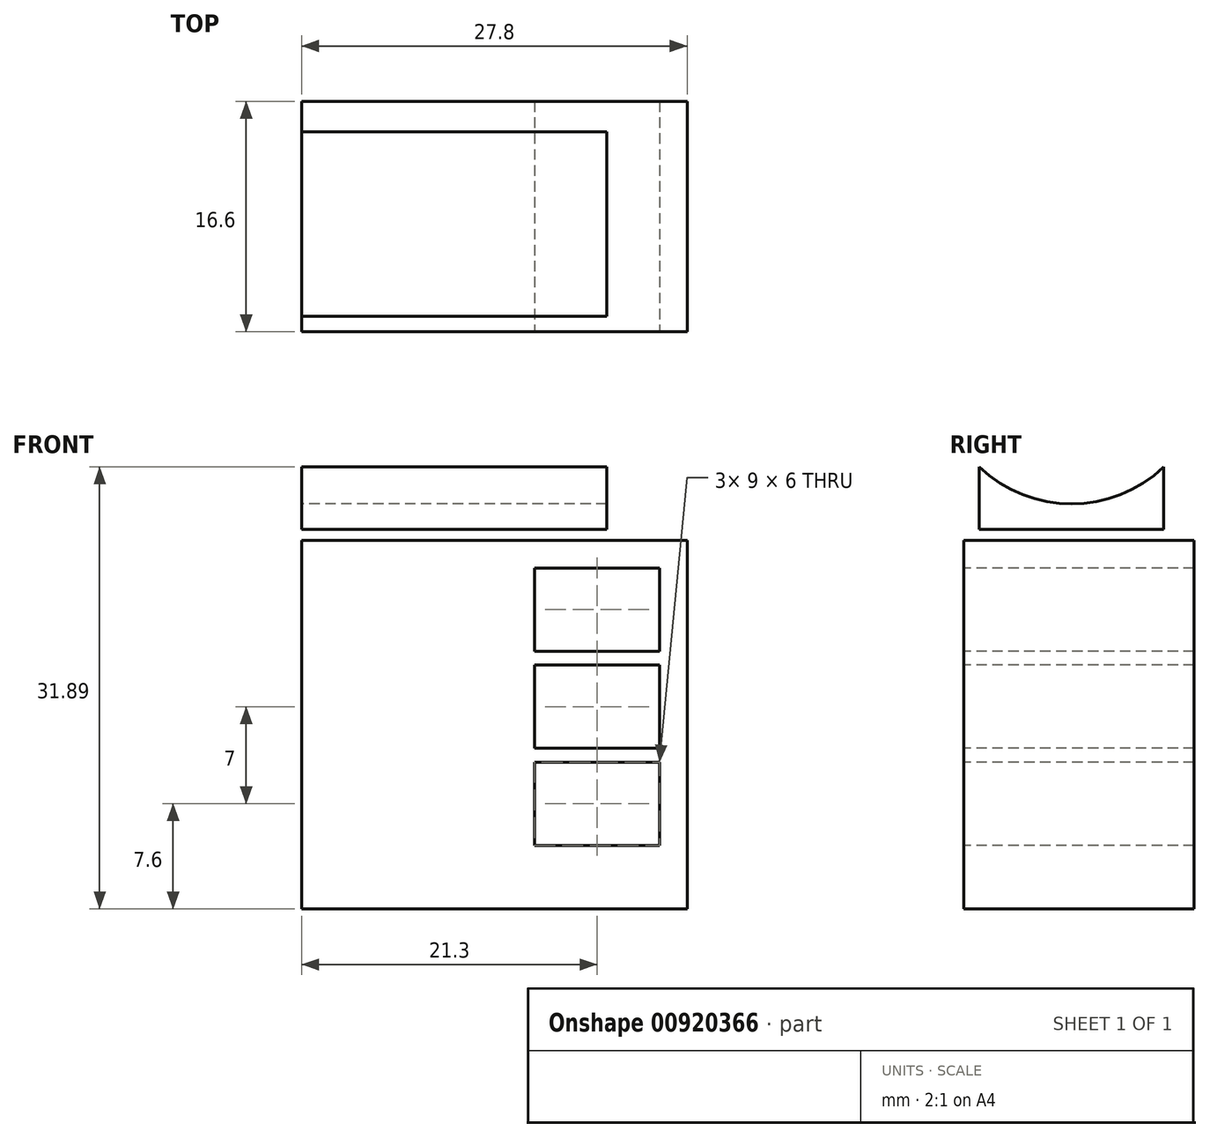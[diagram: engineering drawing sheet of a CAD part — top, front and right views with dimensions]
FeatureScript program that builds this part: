
annotation { "Feature Type Name" : "Feature", "Feature Type Description" : "" }
export const myFeature = defineFeature(function(context is Context, id is Id, definition is map)
    precondition{}
    {
        {
            var Q0;
            Q0=qCreatedBy(makeId("Top.planeOp"),FACE);
            var sketch = newSketch(context, id + "F0", { "sketchPlane" : qUnion([Q0])});
            skLineSegment(sketch, "E0.bottom", {"start": v(0, 16.6) * mm, "end": v(27.8, 16.6) * mm});
            skLineSegment(sketch, "E0.top", {"start": v(0, 0) * mm, "end": v(27.8, 0) * mm});
            skLineSegment(sketch, "E0.left", {"start": v(0, 16.6) * mm, "end": v(0, 0) * mm});
            skLineSegment(sketch, "E0.right", {"start": v(27.8, 16.6) * mm, "end": v(27.8, 0) * mm});
            skSolve(sketch);
        }
        {
            var Q0;
            Q0 = qSketchRegion(id + "F0", true);
            extrude(context, id + "F1", {"entities" : qUnion([Q0]), "depth" : 26.6 * mm, "offsetDistance" : 25 * mm});
        }
        {
            var Q0;
            Q0=makeQuery(id+"F1.opExtrude","SWEPT_FACE",FACE,{"disambiguationData":[OSD([sQuery(id+"F0.wireOp",EDGE,"E0.top")])]});
            var sketch = newSketch(context, id + "F2", { "sketchPlane" : qUnion([Q0])});
            skLineSegment(sketch, "E1.bottom", {"start": v(16.8, 24.6) * mm, "end": v(25.8, 24.6) * mm});
            skLineSegment(sketch, "E1.top", {"start": v(16.8, 18.6) * mm, "end": v(25.8, 18.6) * mm});
            skLineSegment(sketch, "E1.left", {"start": v(16.8, 24.6) * mm, "end": v(16.8, 18.6) * mm});
            skLineSegment(sketch, "E1.right", {"start": v(25.8, 24.6) * mm, "end": v(25.8, 18.6) * mm});
            skLineSegment(sketch, "E2.bottom", {"start": v(16.8, 17.6) * mm, "end": v(25.8, 17.6) * mm});
            skLineSegment(sketch, "E2.top", {"start": v(16.8, 11.6) * mm, "end": v(25.8, 11.6) * mm});
            skLineSegment(sketch, "E2.left", {"start": v(16.8, 17.6) * mm, "end": v(16.8, 11.6) * mm});
            skLineSegment(sketch, "E2.right", {"start": v(25.8, 17.6) * mm, "end": v(25.8, 11.6) * mm});
            skLineSegment(sketch, "E3.bottom", {"start": v(16.8, 10.6) * mm, "end": v(25.8, 10.6) * mm});
            skLineSegment(sketch, "E3.top", {"start": v(16.8, 4.6) * mm, "end": v(25.8, 4.6) * mm});
            skLineSegment(sketch, "E3.left", {"start": v(16.8, 10.6) * mm, "end": v(16.8, 4.6) * mm});
            skLineSegment(sketch, "E3.right", {"start": v(25.8, 10.6) * mm, "end": v(25.8, 4.6) * mm});
            skLineSegment(sketch, "E4", {"start": v(27.8, 26.6) * mm, "end": v(27.8, 2.4) * mm, "construction": true});
            skLineSegment(sketch, "E5", {"start": v(16.67, 26.6) * mm, "end": v(27.8, 26.6) * mm, "construction": true});
            skLineSegment(sketch, "E6", {"start": v(25.8, 24.6) * mm, "end": v(25.8, 26.6) * mm, "construction": true});
            skLineSegment(sketch, "E7", {"start": v(25.8, 24.6) * mm, "end": v(27.8, 24.6) * mm, "construction": true});
            skLineSegment(sketch, "E8", {"start": v(25.8, 17.6) * mm, "end": v(27.8, 17.6) * mm, "construction": true});
            skLineSegment(sketch, "E9", {"start": v(25.8, 10.6) * mm, "end": v(27.8, 10.6) * mm, "construction": true});
            skLineSegment(sketch, "E10", {"start": v(25.8, 17.6) * mm, "end": v(25.8, 18.6) * mm, "construction": true});
            skLineSegment(sketch, "E11", {"start": v(25.8, 10.6) * mm, "end": v(25.8, 11.6) * mm, "construction": true});
            skSolve(sketch);
        }
        {
            var Q0;
            Q0 = qSketchRegion(id + "F2", true);
            extrude(context, id + "F3", {"entities" : qUnion([Q0]), "operationType" : NewBodyOperationType.REMOVE, "oppositeDirection" : true, "depth" : 16.6 * mm, "offsetDistance" : 25 * mm});
        }
        {
            var Q0;
            Q0=qCreatedBy(makeId("Right.planeOp"),FACE);
            var sketch = newSketch(context, id + "F4", { "sketchPlane" : qUnion([Q0])});
            skLineSegment(sketch, "E12", {"start": v(14.42, 27.4) * mm, "end": v(14.42, 31.9) * mm});
            skLineSegment(sketch, "E13", {"start": v(14.42, 27.4) * mm, "end": v(1.12, 27.4) * mm});
            skLineSegment(sketch, "E14", {"start": v(1.12, 27.4) * mm, "end": v(1.12, 31.9) * mm});
            skArc(sketch, "E15", {"start": v(1.12, 31.9) * mm, "mid": v(7.77, 29.22) * mm, "end": v(14.42, 31.9) * mm});
            skSolve(sketch);
        }
        {
            var Q0;
            Q0 = qSketchRegion(id + "F4", true);
            extrude(context, id + "F5", {"entities" : qUnion([Q0]), "depth" : 22 * mm, "offsetDistance" : 25 * mm});
        }
    });
